# Revit family: Specialty Equipment_Grab Rail_Metlam_Ambulant 90_MLR1128621423f-cf8f-4a4d-a26c-7caf784a56a2
name_source: partatom
category: Specialty Equipment
revit_build: Autodesk Revit 2014 (Build: 20130308_1515(x64)
units: mm (PartAtom-declared; Revit-internal decimal feet)

## types (1)
- 450l x 450h x 60d
    Assembly Code = C1030200
    Description = 90° Ambulant Grab Rail
    Manufacturer = Metlam
    Manufacturer_Overall Depth = 60 mm  [stored 0.19685 ft]
    Manufacturer_Overall Height = 450 mm  [stored 1.47638 ft]
    Manufacturer_Overall Width = 450 mm  [stored 1.47638 ft]
    Manufacturer_Spec Code = MLR112
    Manufacturer_URL__Product Specific = http://www.metlam.com.au
    Material = z_Metlam_Metal_Stainless Steel Satin
    Model = MLR112
    ModifiedIssue_ANZRS = 20150202 $
    Type Comments = MLR112
    URL = www.metlam.com.au

note: [stored X ft] marks values corroborated as IEEE doubles in the binary element streams (Revit-internal decimal feet)

## geometry (parser evidence)
native form markers: Sweep x1
no freeform markers — native parametric forms only
